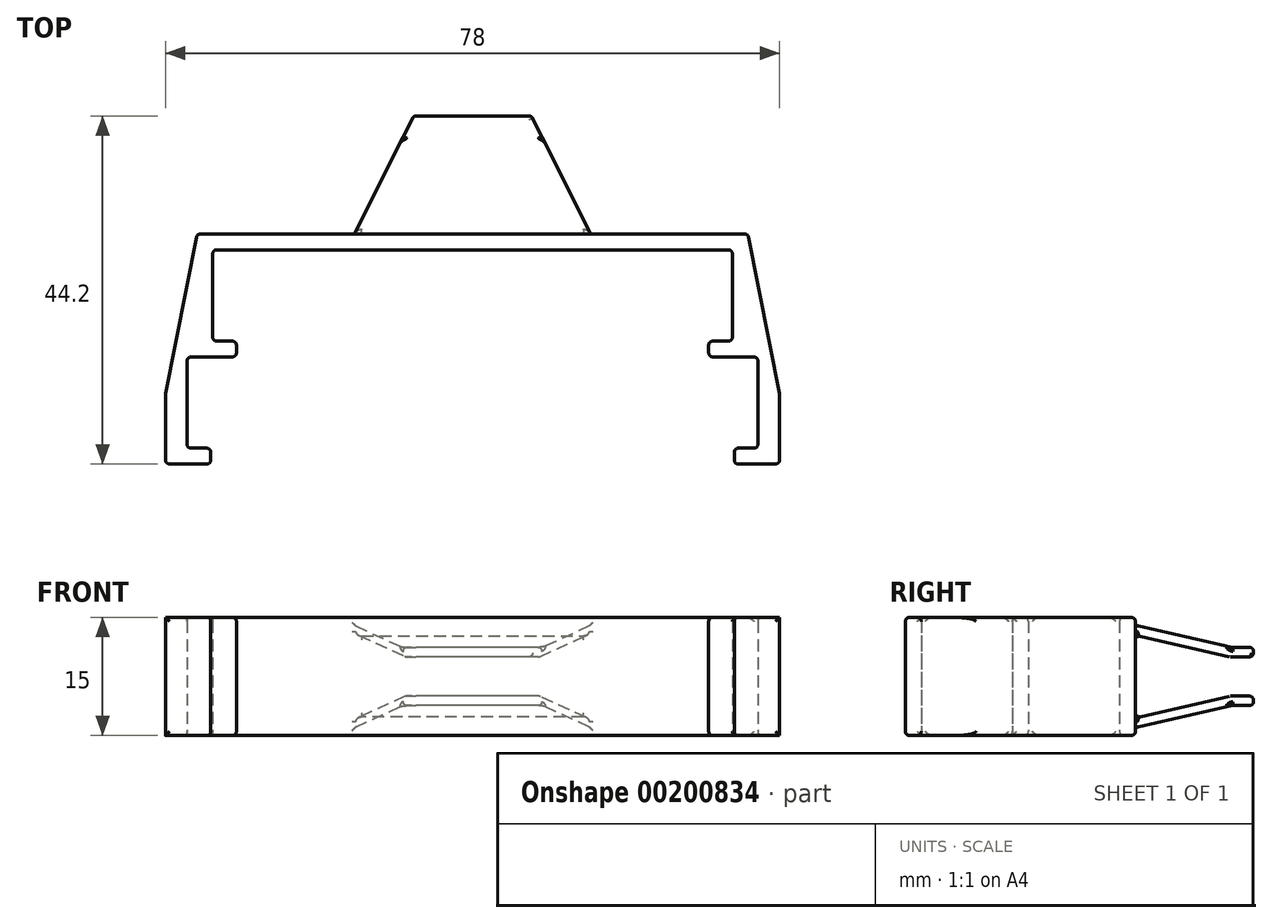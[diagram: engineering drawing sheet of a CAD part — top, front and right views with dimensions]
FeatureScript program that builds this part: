
annotation { "Feature Type Name" : "Feature", "Feature Type Description" : "" }
export const myFeature = defineFeature(function(context is Context, id is Id, definition is map)
    precondition{}
    {
        {
            var Q0;
            Q0=qCreatedBy(makeId("Top.planeOp"),FACE);
            var sketch = newSketch(context, id + "F0", { "sketchPlane" : qUnion([Q0])});
            skLineSegment(sketch, "E0", {"start": v(33, 13.6) * mm, "end": v(33, 2) * mm});
            skLineSegment(sketch, "E1", {"start": v(33, 2) * mm, "end": v(30, 2) * mm});
            skLineSegment(sketch, "E2", {"start": v(30, 2) * mm, "end": v(30, 0) * mm});
            skLineSegment(sketch, "E3", {"start": v(30, 0) * mm, "end": v(36.25, 0) * mm});
            skLineSegment(sketch, "E4", {"start": v(36.25, 0) * mm, "end": v(36.25, -11.6) * mm});
            skLineSegment(sketch, "E5", {"start": v(36.25, -11.6) * mm, "end": v(33.25, -11.6) * mm});
            skLineSegment(sketch, "E6", {"start": v(33.25, -11.6) * mm, "end": v(33.25, -13.6) * mm});
            skLineSegment(sketch, "E7", {"start": v(33.25, -13.6) * mm, "end": v(40.75, -13.6) * mm});
            skLineSegment(sketch, "E8", {"start": v(40.75, -13.6) * mm, "end": v(35, 15.6) * mm});
            skLineSegment(sketch, "E9", {"start": v(0, 0) * mm, "end": v(0, 35.07) * mm, "construction": true});
            skLineSegment(sketch, "E10.MirrorCS", {"start": v(-33.25, -11.6) * mm, "end": v(-33.25, -13.6) * mm});
            skLineSegment(sketch, "E11.MirrorCS", {"start": v(-30, 2) * mm, "end": v(-30, 0) * mm});
            skLineSegment(sketch, "E12.MirrorCS", {"start": v(-33, 13.6) * mm, "end": v(-33, 2) * mm});
            skLineSegment(sketch, "E13.MirrorCS", {"start": v(-40.75, -13.6) * mm, "end": v(-35, 15.6) * mm});
            skLineSegment(sketch, "E14.MirrorCS", {"start": v(-33, 2) * mm, "end": v(-30, 2) * mm});
            skLineSegment(sketch, "E15.MirrorCS", {"start": v(-36.25, -11.6) * mm, "end": v(-33.25, -11.6) * mm});
            skLineSegment(sketch, "E16.MirrorCS", {"start": v(-33.25, -13.6) * mm, "end": v(-40.75, -13.6) * mm});
            skLineSegment(sketch, "E17.MirrorCS", {"start": v(-36.25, 0) * mm, "end": v(-36.25, -11.6) * mm});
            skLineSegment(sketch, "E18.MirrorCS", {"start": v(-30, 0) * mm, "end": v(-36.25, 0) * mm});
            skLineSegment(sketch, "E19", {"start": v(-35, 15.6) * mm, "end": v(35, 15.6) * mm});
            skLineSegment(sketch, "E20", {"start": v(33, 13.6) * mm, "end": v(-33, 13.6) * mm});
            skSolve(sketch);
        }
        {
            var Q0;
            Q0=makeQuery(id+"F0.imprint","IMPRINT",FACE,{"disambiguationData":[TD([[makeQuery(id+"F0.imprint","IMPRINT",EDGE,{"derivedFrom":sQuery(id+"F0.wireOp",EDGE,"E0")}),1.0]])]});
            extrude(context, id + "F1", {"entities" : qUnion([Q0]), "endBound" : BoundingType.SYMMETRIC, "depth" : 15 * mm});
        }
        {
            var Q0;
            Q0=qCreatedBy(makeId("Right.planeOp"),FACE);
            var sketch = newSketch(context, id + "F2", { "sketchPlane" : qUnion([Q0])});
            skLineSegment(sketch, "E21", {"start": v(0, 0) * mm, "end": v(47.63, 0) * mm, "construction": true});
            skLineSegment(sketch, "E22", {"start": v(15.6, 6.48) * mm, "end": v(27.74, 3.7) * mm});
            skLineSegment(sketch, "E23", {"start": v(27.6, 2.5) * mm, "end": v(15.6, 5.25) * mm});
            skLineSegment(sketch, "E24", {"start": v(15.6, 6.48) * mm, "end": v(15.6, 0) * mm, "construction": true});
            skLineSegment(sketch, "E25.bottom", {"start": v(27.6, 2.5) * mm, "end": v(30.6, 2.5) * mm});
            skLineSegment(sketch, "E25.top", {"start": v(27.74, 3.7) * mm, "end": v(30.6, 3.7) * mm});
            skLineSegment(sketch, "E25.right", {"start": v(30.6, 2.5) * mm, "end": v(30.6, 3.7) * mm});
            skLineSegment(sketch, "E26", {"start": v(15.6, 6.48) * mm, "end": v(15.6, 5.25) * mm});
            skLineSegment(sketch, "E27.MirrorCS", {"start": v(15.6, -6.48) * mm, "end": v(15.6, -5.25) * mm});
            skLineSegment(sketch, "E28.MirrorCS", {"start": v(27.6, -2.5) * mm, "end": v(30.6, -2.5) * mm});
            skLineSegment(sketch, "E29.MirrorCS", {"start": v(27.6, -2.5) * mm, "end": v(15.6, -5.25) * mm});
            skLineSegment(sketch, "E30.MirrorCS", {"start": v(15.6, -6.48) * mm, "end": v(27.74, -3.7) * mm});
            skLineSegment(sketch, "E31.MirrorCS", {"start": v(30.6, -2.5) * mm, "end": v(30.6, -3.7) * mm});
            skLineSegment(sketch, "E32.MirrorCS", {"start": v(27.74, -3.7) * mm, "end": v(30.6, -3.7) * mm});
            skSolve(sketch);
        }
        {
            var Q0;
            Q0=makeQuery(id+"F2.imprint","IMPRINT",FACE,{"disambiguationData":[TD([[makeQuery(id+"F2.imprint","IMPRINT",EDGE,{"derivedFrom":sQuery(id+"F2.wireOp",EDGE,"E27.MirrorCS")}),-1.0]])]});
            var Q1;
            Q1=makeQuery(id+"F2.imprint","IMPRINT",FACE,{"disambiguationData":[TD([[makeQuery(id+"F2.imprint","IMPRINT",EDGE,{"derivedFrom":sQuery(id+"F2.wireOp",EDGE,"E22")}),-1.0]])]});
            extrude(context, id + "F3", {"entities" : qUnion([Q0, Q1]), "operationType" : NewBodyOperationType.ADD, "endBound" : BoundingType.SYMMETRIC, "depth" : 30 * mm});
        }
        {
            var Q0;
            Q0=makeQuery(id+"F1.opExtrude","CAP_FACE",FACE,{"disambiguationData":[OSD([sQuery(id+"F0.wireOp",EDGE,"E0"),sQuery(id+"F0.wireOp",EDGE,"E1"),sQuery(id+"F0.wireOp",EDGE,"E2"),sQuery(id+"F0.wireOp",EDGE,"E3"),sQuery(id+"F0.wireOp",EDGE,"E4"),sQuery(id+"F0.wireOp",EDGE,"E5"),sQuery(id+"F0.wireOp",EDGE,"E6"),sQuery(id+"F0.wireOp",EDGE,"E7"),sQuery(id+"F0.wireOp",EDGE,"E8"),sQuery(id+"F0.wireOp",EDGE,"E10.MirrorCS"),sQuery(id+"F0.wireOp",EDGE,"E11.MirrorCS"),sQuery(id+"F0.wireOp",EDGE,"E12.MirrorCS"),sQuery(id+"F0.wireOp",EDGE,"E13.MirrorCS"),sQuery(id+"F0.wireOp",EDGE,"E14.MirrorCS"),sQuery(id+"F0.wireOp",EDGE,"E15.MirrorCS"),sQuery(id+"F0.wireOp",EDGE,"E16.MirrorCS"),sQuery(id+"F0.wireOp",EDGE,"E17.MirrorCS"),sQuery(id+"F0.wireOp",EDGE,"E18.MirrorCS"),sQuery(id+"F0.wireOp",EDGE,"E19"),sQuery(id+"F0.wireOp",EDGE,"E20")])],"isStart":false});
            var sketch = newSketch(context, id + "F4", { "sketchPlane" : qUnion([Q0])});
            skLineSegment(sketch, "E33", {"start": v(0, 15.6) * mm, "end": v(0, 30.6) * mm, "construction": true});
            skPoint(sketch, "E34.endSnap0", {"position": v(0, 23.1) * mm});
            skLineSegment(sketch, "E35", {"start": v(0, 30.6) * mm, "end": v(7.5, 30.6) * mm});
            skLineSegment(sketch, "E36", {"start": v(0, 15.6) * mm, "end": v(15, 15.6) * mm});
            skLineSegment(sketch, "E37", {"start": v(15, 15.6) * mm, "end": v(7.5, 30.6) * mm});
            skLineSegment(sketch, "E38.MirrorCS", {"start": v(0, 15.6) * mm, "end": v(-15, 15.6) * mm});
            skLineSegment(sketch, "E39.MirrorCS", {"start": v(0, 30.6) * mm, "end": v(-7.5, 30.6) * mm});
            skLineSegment(sketch, "E40.MirrorCS", {"start": v(-15, 15.6) * mm, "end": v(-7.5, 30.6) * mm});
            skLineSegment(sketch, "E41.bottom", {"start": v(39, 15.6) * mm, "end": v(-39, 15.6) * mm});
            skLineSegment(sketch, "E41.top", {"start": v(39, -15.6) * mm, "end": v(-39, -15.6) * mm});
            skLineSegment(sketch, "E41.left", {"start": v(39, 15.6) * mm, "end": v(39, -15.6) * mm});
            skLineSegment(sketch, "E41.right", {"start": v(-39, 15.6) * mm, "end": v(-39, -15.6) * mm});
            skPoint(sketch, "E41.middle", {"position": v(0, 0) * mm});
            skSolve(sketch);
        }
        {
            var Q0;
            Q0=qSketchRegion(id+"F4",true);
            extrude(context, id + "F5", {"entities" : qUnion([Q0]), "operationType" : NewBodyOperationType.INTERSECT, "oppositeDirection" : true, "depth" : 15 * mm});
        }
        {
            var Q0;
            Q0=makeQuery(id+"F3.opExtrude","SWEPT_FACE",FACE,{"disambiguationData":[OSD([sQuery(id+"F2.wireOp",EDGE,"E25.right")])]});
            var Q1;
            Q1=makeQuery(id+"F3.opExtrude","SWEPT_FACE",FACE,{"disambiguationData":[OSD([sQuery(id+"F2.wireOp",EDGE,"E31.MirrorCS")])]});
            var Q2;
            Q2=makeQuery(id+"F3.opExtrude","SWEPT_FACE",FACE,{"disambiguationData":[OSD([sQuery(id+"F2.wireOp",EDGE,"E28.MirrorCS")])]});
            var Q3;
            Q3=makeQuery(id+"F3.opExtrude","SWEPT_FACE",FACE,{"disambiguationData":[OSD([sQuery(id+"F2.wireOp",EDGE,"E25.top")])]});
            var Q4;
            Q4=makeQuery(id+"F3.opExtrude","SWEPT_FACE",FACE,{"disambiguationData":[OSD([sQuery(id+"F2.wireOp",EDGE,"E32.MirrorCS")])]});
            var Q5;
            Q5=makeQuery(id+"F3.opExtrude","SWEPT_FACE",FACE,{"disambiguationData":[OSD([sQuery(id+"F2.wireOp",EDGE,"E25.bottom")])]});
            var Q6;
            Q6=makeQuery(id+"F3.opExtrude","SWEPT_FACE",FACE,{"disambiguationData":[OSD([sQuery(id+"F2.wireOp",EDGE,"E23")])]});
            var Q7;
            Q7=makeQuery(id+"F3.opExtrude","SWEPT_FACE",FACE,{"disambiguationData":[OSD([sQuery(id+"F2.wireOp",EDGE,"E29.MirrorCS")])]});
            var Q8;
            Q8=makeQuery(id+"F1.opExtrude","SWEPT_FACE",FACE,{"disambiguationData":[OSD([sQuery(id+"F0.wireOp",EDGE,"E20")])]});
            var Q9;
            Q9=makeQuery(id+"F1.opExtrude","SWEPT_FACE",FACE,{"disambiguationData":[OSD([sQuery(id+"F0.wireOp",EDGE,"E18.MirrorCS")])]});
            var Q10;
            Q10=makeQuery(id+"F1.opExtrude","SWEPT_EDGE",EDGE,{"disambiguationData":[OSD([sQuery(id+"F0.wireOp",EDGE,"E11.MirrorCS"),sQuery(id+"F0.wireOp",EDGE,"E14.MirrorCS")])]});
            var Q11;
            Q11=makeQuery(id+"F1.opExtrude","SWEPT_FACE",FACE,{"disambiguationData":[OSD([sQuery(id+"F0.wireOp",EDGE,"E15.MirrorCS")])]});
            var Q12;
            Q12=makeQuery(id+"F1.opExtrude","SWEPT_FACE",FACE,{"disambiguationData":[OSD([sQuery(id+"F0.wireOp",EDGE,"E14.MirrorCS")])]});
            var Q13;
            Q13=makeQuery(id+"F1.opExtrude","SWEPT_FACE",FACE,{"disambiguationData":[OSD([sQuery(id+"F0.wireOp",EDGE,"E10.MirrorCS")])]});
            var Q14;
            Q14=makeQuery(id+"F1.opExtrude","SWEPT_FACE",FACE,{"disambiguationData":[OSD([sQuery(id+"F0.wireOp",EDGE,"E11.MirrorCS")])]});
            var Q15;
            Q15=makeQuery(id+"F1.opExtrude","SWEPT_FACE",FACE,{"disambiguationData":[OSD([sQuery(id+"F0.wireOp",EDGE,"E4")])]});
            var Q16;
            Q16=makeQuery(id+"F1.opExtrude","SWEPT_FACE",FACE,{"disambiguationData":[OSD([sQuery(id+"F0.wireOp",EDGE,"E1")])]});
            var Q17;
            Q17=makeQuery(id+"F1.opExtrude","SWEPT_FACE",FACE,{"disambiguationData":[OSD([sQuery(id+"F0.wireOp",EDGE,"E6")])]});
            var Q18;
            Q18=makeQuery(id+"F1.opExtrude","SWEPT_FACE",FACE,{"disambiguationData":[OSD([sQuery(id+"F0.wireOp",EDGE,"E2")])]});
            var Q19;
            Q19=makeQuery(id+"F5.boolean.opBoolean","COPY",FACE,{"derivedFrom":makeQuery(id+"F5.boolean.toolComplement.opBoolean","COPY",FACE,{"derivedFrom":makeQuery(id+"F5.opExtrude","SWEPT_FACE",FACE,{"disambiguationData":[OSD([sQuery(id+"F4.wireOp",EDGE,"E41.right")])]})})});
            var Q20;
            Q20=makeQuery(id+"F1.opExtrude","SWEPT_FACE",FACE,{"disambiguationData":[OSD([sQuery(id+"F0.wireOp",EDGE,"E13.MirrorCS")])]});
            var Q21;
            Q21=makeQuery(id+"F1.opExtrude","SWEPT_FACE",FACE,{"disambiguationData":[OSD([sQuery(id+"F0.wireOp",EDGE,"E16.MirrorCS")])]});
            var Q22;
            Q22=makeQuery(id+"F5.boolean.opBoolean","COPY",FACE,{"derivedFrom":makeQuery(id+"F5.boolean.toolComplement.opBoolean","COPY",FACE,{"derivedFrom":makeQuery(id+"F5.opExtrude","SWEPT_FACE",FACE,{"disambiguationData":[OSD([sQuery(id+"F4.wireOp",EDGE,"E41.left")])]})})});
            var Q23;
            Q23=makeQuery(id+"F1.opExtrude","SWEPT_FACE",FACE,{"disambiguationData":[OSD([sQuery(id+"F0.wireOp",EDGE,"E7")])]});
            var Q24;
            Q24=makeQuery(id+"F1.opExtrude","SWEPT_FACE",FACE,{"disambiguationData":[OSD([sQuery(id+"F0.wireOp",EDGE,"E8")])]});
            var Q25;
            Q25=makeQuery(id+"F1.opExtrude","SWEPT_FACE",FACE,{"disambiguationData":[OSD([sQuery(id+"F0.wireOp",EDGE,"E19")])]});
            fillet(context, id + "F6", {"entities" : qUnion([Q0, Q1, Q2, Q3, Q4, Q5, Q6, Q7, Q8, Q9, Q10, Q11, Q12, Q13, Q14, Q15, Q16, Q17, Q18, Q19, Q20, Q21, Q22, Q23, Q24, Q25]), "radius" : 0.5 * mm, "tangentPropagation" : true, "allowEdgeOverflow" : false});
        }
    });
